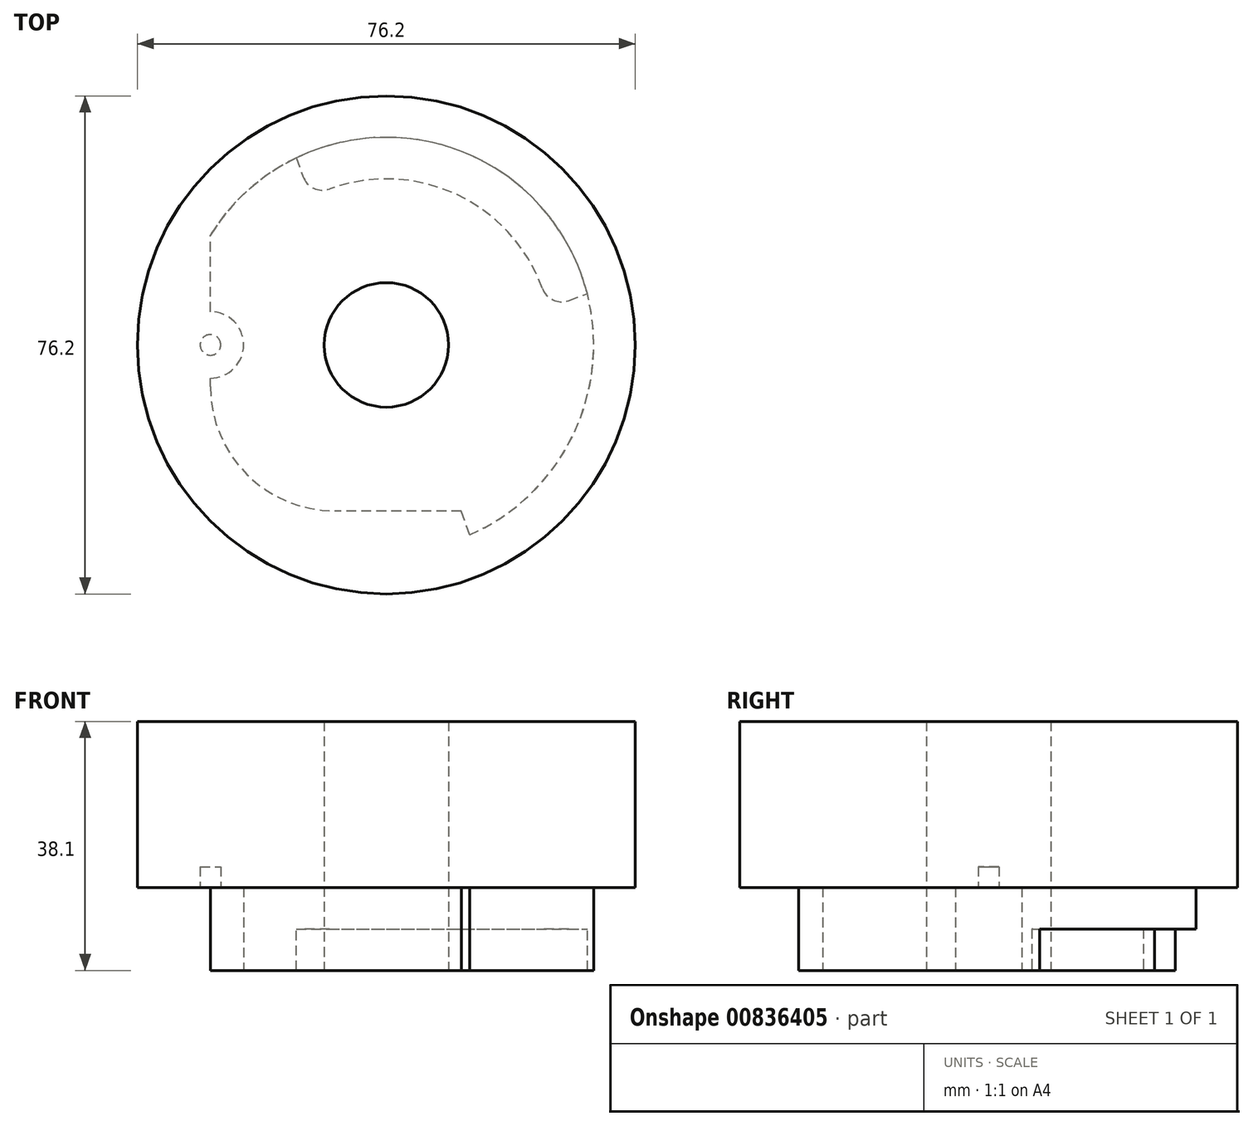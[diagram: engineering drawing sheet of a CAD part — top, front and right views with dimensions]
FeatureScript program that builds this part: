
annotation { "Feature Type Name" : "Feature", "Feature Type Description" : "" }
export const myFeature = defineFeature(function(context is Context, id is Id, definition is map)
    precondition{}
    {
        {
            var Q0;
            Q0=qCreatedBy(makeId("Front.planeOp"),FACE);
            var sketch = newSketch(context, id + "F0", { "sketchPlane" : qUnion([Q0])});
            skLineSegment(sketch, "E0", {"start": v(31.75, 0) * mm, "end": v(31.75, 12.7) * mm});
            skLineSegment(sketch, "E1", {"start": v(31.75, 12.7) * mm, "end": v(38.1, 12.7) * mm});
            skLineSegment(sketch, "E2", {"start": v(38.1, 12.7) * mm, "end": v(38.1, 38.1) * mm});
            skLineSegment(sketch, "E3", {"start": v(38.1, 38.1) * mm, "end": v(0, 38.1) * mm});
            skLineSegment(sketch, "E4", {"start": v(0, 38.1) * mm, "end": v(0, 0) * mm});
            skLineSegment(sketch, "E5", {"start": v(0, 0) * mm, "end": v(31.75, 0) * mm});
            skSolve(sketch);
        }
        {
            var Q0;
            Q0=makeQuery(id+"F0.imprint","IMPRINT",FACE,{"disambiguationData":[TD([[makeQuery(id+"F0.imprint","IMPRINT",EDGE,{"derivedFrom":sQuery(id+"F0.wireOp",EDGE,"E0")}),1.0]])]});
            var Q1;
            Q1=sQuery(id+"F0.wireOp",EDGE,"E4");
            revolve(context, id + "F1", {"surfaceOperationType" : NewSurfaceOperationType.NEW, "entities" : qUnion([Q0]), "axis" : qUnion([Q1]), "revolveType" : RevolveType.FULL});
        }
        {
            var Q0;
            Q0=makeQuery(id+"F1.opRevolve","SWEPT_FACE",FACE,{"disambiguationData":[OSD([sQuery(id+"F0.wireOp",EDGE,"E5")])]});
            var sketch = newSketch(context, id + "F2", { "sketchPlane" : qUnion([Q0])});
            skLineSegment(sketch, "E6", {"start": v(12.76, 29.07) * mm, "end": v(11.48, 25.4) * mm});
            skLineSegment(sketch, "E7", {"start": v(11.48, 25.4) * mm, "end": v(-7.87, 25.4) * mm});
            skArc(sketch, "E8", {"start": v(-7.87, 25.4) * mm, "mid": v(-21.34, 19.82) * mm, "end": v(-26.92, 6.35) * mm});
            skLineSegment(sketch, "E9", {"start": v(-26.92, 6.35) * mm, "end": v(-7.87, 6.35) * mm, "construction": true});
            skLineSegment(sketch, "E10", {"start": v(-48.72, -19.05) * mm, "end": v(-32.54, 29.23) * mm});
            skLineSegment(sketch, "E11", {"start": v(-32.54, 29.23) * mm, "end": v(20.22, 33.7) * mm});
            skLineSegment(sketch, "E12", {"start": v(20.22, 33.7) * mm, "end": v(12.76, 29.07) * mm});
            skLineSegment(sketch, "E13", {"start": v(-26.92, 6.35) * mm, "end": v(-26.92, 5.08) * mm});
            skLineSegment(sketch, "E14", {"start": v(-26.92, -19.05) * mm, "end": v(-48.72, -19.05) * mm});
            skArc(sketch, "E15", {"start": v(-26.92, -5.08) * mm, "mid": v(-21.84, 0) * mm, "end": v(-26.92, 5.08) * mm});
            skLineSegment(sketch, "E16.trimOffspring", {"start": v(-26.92, -5.08) * mm, "end": v(-26.92, -19.05) * mm});
            skSolve(sketch);
        }
        {
            var Q0;
            Q0 = qSketchRegion(id + "F2", true);
            extrude(context, id + "F3", {"entities" : qUnion([Q0]), "operationType" : NewBodyOperationType.REMOVE, "oppositeDirection" : true, "depth" : 12.7 * mm, "offsetDistance" : 25.4 * mm});
        }
        {
            var Q0;
            Q0=makeQuery(id+"F1.opRevolve","SWEPT_FACE",FACE,{"disambiguationData":[OSD([sQuery(id+"F0.wireOp",EDGE,"E5")])]});
            var sketch = newSketch(context, id + "F4", { "sketchPlane" : qUnion([Q0])});
            skArc(sketch, "E17", {"start": v(-8.69, -23.87) * mm, "mid": v(10.73, -23.02) * mm, "end": v(23.87, -8.69) * mm});
            skLineSegment(sketch, "E18", {"start": v(-8.69, -23.87) * mm, "end": v(0, 0) * mm, "construction": true});
            skLineSegment(sketch, "E19", {"start": v(0, 0) * mm, "end": v(23.87, -8.69) * mm, "construction": true});
            skArc(sketch, "E20", {"start": v(23.87, -8.69) * mm, "mid": v(25.5, -6.9) * mm, "end": v(27.94, -6.79) * mm});
            skArc(sketch, "E21", {"start": v(-8.69, -23.87) * mm, "mid": v(-11.12, -23.97) * mm, "end": v(-12.76, -25.77) * mm});
            skLineSegment(sketch, "E22", {"start": v(27.94, -6.79) * mm, "end": v(61.93, -19.16) * mm});
            skLineSegment(sketch, "E23", {"start": v(61.93, -19.16) * mm, "end": v(-28.88, -70.06) * mm});
            skLineSegment(sketch, "E24", {"start": v(-28.88, -70.06) * mm, "end": v(-12.76, -25.77) * mm});
            skSolve(sketch);
        }
        {
            var Q0;
            Q0 = qSketchRegion(id + "F4", true);
            extrude(context, id + "F5", {"entities" : qUnion([Q0]), "operationType" : NewBodyOperationType.REMOVE, "oppositeDirection" : true, "depth" : 6.35 * mm, "offsetDistance" : 25.4 * mm});
        }
        {
            var Q0;
            Q0=makeQuery(id+"F1.opRevolve","SWEPT_FACE",FACE,{"disambiguationData":[OSD([sQuery(id+"F0.wireOp",EDGE,"E5")])]});
            var sketch = newSketch(context, id + "F6", { "sketchPlane" : qUnion([Q0])});
            skPoint(sketch, "E25", {"position": v(0, 0) * mm});
            skSolve(sketch);
        }
        {
            var Q0;
            Q0=sQuery(id+"F6.wireOp",VERTEX,"E25");
            var Q1;
            Q1=makeQuery(id+"F1.opRevolve","SWEPT_BODY",BODY,{"disambiguationData":[OSD([sQuery(id+"F0.wireOp",EDGE,"E0"),sQuery(id+"F0.wireOp",EDGE,"E1"),sQuery(id+"F0.wireOp",EDGE,"E2"),sQuery(id+"F0.wireOp",EDGE,"E3"),sQuery(id+"F0.wireOp",EDGE,"E4"),sQuery(id+"F0.wireOp",EDGE,"E5")])]});
            hole(context, id + "F7", {"style" : HoleStyle.SIMPLE, "endStyle" : HoleEndStyle.THROUGH, "holeDiameter" : 19.05 * mm, "majorDiameter" : 6.35 * mm, "isTappedThrough" : true, "tappedDepth" : 50.8 * mm, "tapClearance" : 3, "locations" : qUnion([Q0]), "scope" : qUnion([Q1])});
        }
        {
            var Q0;
            Q0=makeQuery(id+"F3.boolean.opBoolean","MERGE",FACE,{"derivedFrom":[makeQuery(id+"F1.opRevolve","SWEPT_FACE",FACE,{"disambiguationData":[OSD([sQuery(id+"F0.wireOp",EDGE,"E1")])]}),makeQuery(id+"F3.opExtrude","CAP_FACE",FACE,{"disambiguationData":[OSD([sQuery(id+"F2.wireOp",EDGE,"E6"),sQuery(id+"F2.wireOp",EDGE,"E7"),sQuery(id+"F2.wireOp",EDGE,"E8"),sQuery(id+"F2.wireOp",EDGE,"E10"),sQuery(id+"F2.wireOp",EDGE,"E11"),sQuery(id+"F2.wireOp",EDGE,"E12"),sQuery(id+"F2.wireOp",EDGE,"E13"),sQuery(id+"F2.wireOp",EDGE,"E14"),sQuery(id+"F2.wireOp",EDGE,"E15"),sQuery(id+"F2.wireOp",EDGE,"E16.trimOffspring")])],"isStart":false})]});
            var Q1;
            Q1=makeQuery(id+"F3.boolean.opBoolean","MERGE",FACE,{"derivedFrom":[makeQuery(id+"F1.opRevolve","SWEPT_FACE",FACE,{"disambiguationData":[OSD([sQuery(id+"F0.wireOp",EDGE,"E1")])]}),makeQuery(id+"F3.opExtrude","CAP_FACE",FACE,{"disambiguationData":[OSD([sQuery(id+"F2.wireOp",EDGE,"E6"),sQuery(id+"F2.wireOp",EDGE,"E7"),sQuery(id+"F2.wireOp",EDGE,"E8"),sQuery(id+"F2.wireOp",EDGE,"E10"),sQuery(id+"F2.wireOp",EDGE,"E11"),sQuery(id+"F2.wireOp",EDGE,"E12"),sQuery(id+"F2.wireOp",EDGE,"E13"),sQuery(id+"F2.wireOp",EDGE,"E14"),sQuery(id+"F2.wireOp",EDGE,"E15"),sQuery(id+"F2.wireOp",EDGE,"E16.trimOffspring")])],"isStart":false})]});
            var sketch = newSketch(context, id + "F8", { "sketchPlane" : qUnion([Q0, Q1])});
            skCircle(sketch, "E26", {"center": v(-26.92, 0) * mm, "radius": 1.59 * mm});
            skSolve(sketch);
        }
        {
            var Q0;
            Q0 = qSketchRegion(id + "F8", true);
            extrude(context, id + "F9", {"entities" : qUnion([Q0]), "operationType" : NewBodyOperationType.REMOVE, "oppositeDirection" : true, "depth" : 3.17 * mm, "offsetDistance" : 25.4 * mm});
        }
    });
